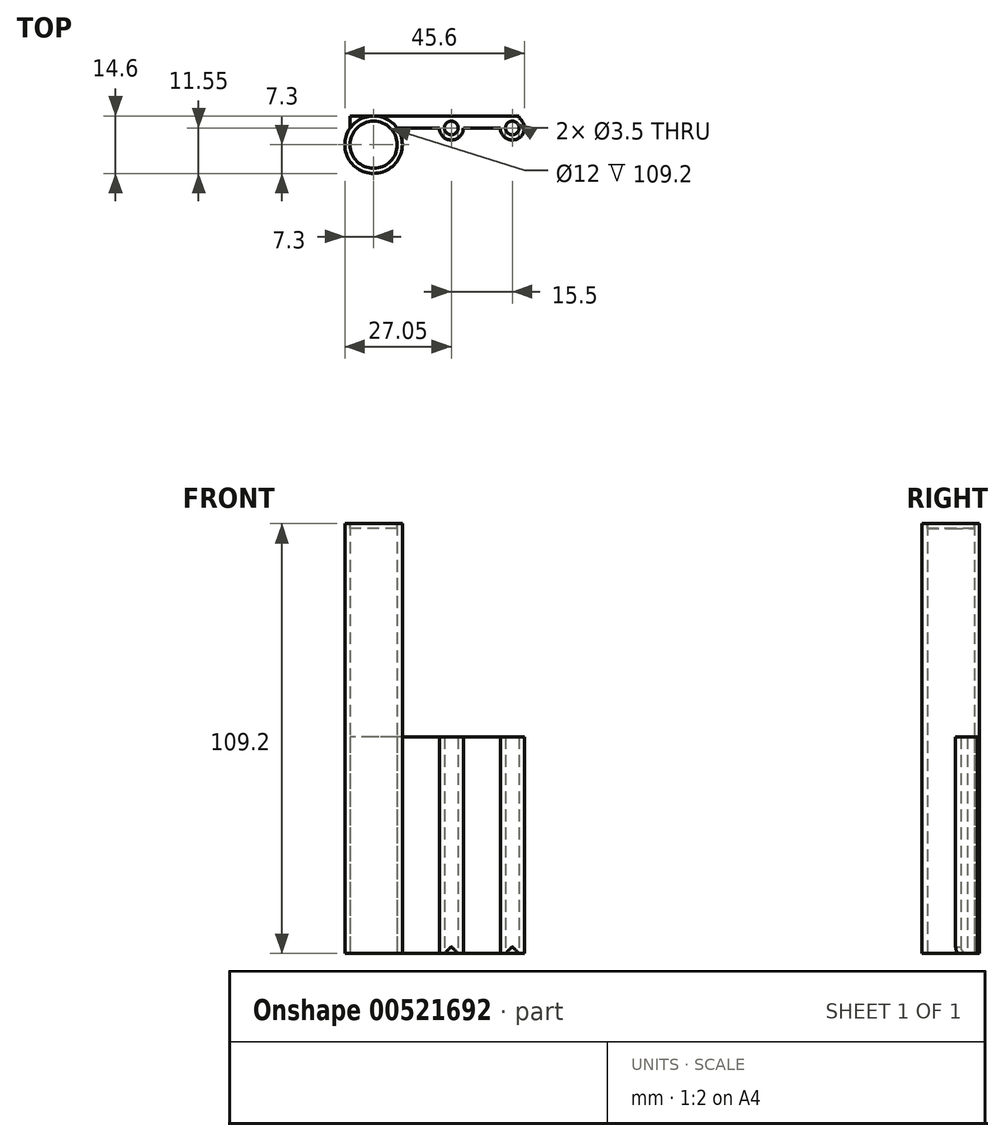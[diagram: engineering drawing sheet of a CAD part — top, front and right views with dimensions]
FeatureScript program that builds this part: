
annotation { "Feature Type Name" : "Feature", "Feature Type Description" : "" }
export const myFeature = defineFeature(function(context is Context, id is Id, definition is map)
    precondition{}
    {
        {
            var Q0;
            Q0=qCreatedBy(makeId("Top.planeOp"),FACE);
            var sketch = newSketch(context, id + "F0", { "sketchPlane" : qUnion([Q0])});
            skLineSegment(sketch, "E0.MirrorCS", {"start": v(-1.3, -1.75) * mm, "end": v(-1.3, -1.84) * mm});
            skLineSegment(sketch, "E1.MirrorCS", {"start": v(29.7, 0.75) * mm, "end": v(29.7, 1.3) * mm});
            skLineSegment(sketch, "E2.MirrorCS", {"start": v(9.4, -1.75) * mm, "end": v(-1.3, -1.75) * mm});
            skLineSegment(sketch, "E3.MirrorCS", {"start": v(-13.3, -1.84) * mm, "end": v(-13.3, 1.3) * mm});
            skArc(sketch, "E4.MirrorCS", {"start": v(-1.3, -1.84) * mm, "mid": v(-7.3, -13.3) * mm, "end": v(-13.3, -1.84) * mm});
            skCircle(sketch, "E5.MirrorC", {"center": v(-7.3, -6) * mm, "radius": 6 * mm});
            skLineSegment(sketch, "E6.MirrorCS", {"start": v(24.9, -1.75) * mm, "end": v(15.5, -1.75) * mm});
            skArc(sketch, "E7.MirrorCS", {"start": v(29.7, 0.75) * mm, "mid": v(29.36, -4.46) * mm, "end": v(24.9, -1.75) * mm});
            skLineSegment(sketch, "E8.MirrorCS", {"start": v(29.7, 1.3) * mm, "end": v(-13.3, 1.3) * mm});
            skCircle(sketch, "E9.MirrorC", {"center": v(27.95, -1.75) * mm, "radius": 1.75 * mm});
            skCircle(sketch, "E10.MirrorC", {"center": v(12.45, -1.75) * mm, "radius": 1.75 * mm});
            skArc(sketch, "E11.MirrorCS", {"start": v(9.4, -1.75) * mm, "mid": v(12.45, -4.8) * mm, "end": v(15.5, -1.75) * mm});
            skSolve(sketch);
        }
        {
            var Q0;
            Q0 = qSketchRegion(id + "F0", true);
            extrude(context, id + "F1", {"entities" : qUnion([Q0]), "depth" : 109.2 * mm, "offsetDistance" : 25 * mm});
        }
        {
            var Q0;
            Q0=makeQuery(id+"F1.opExtrude","SWEPT_FACE",FACE,{"disambiguationData":[OSD([sQuery(id+"F0.wireOp",EDGE,"E2.MirrorCS")])]});
            var sketch = newSketch(context, id + "F2", { "sketchPlane" : qUnion([Q0])});
            skLineSegment(sketch, "E12", {"start": v(10.7, 0) * mm, "end": v(12.45, 1.75) * mm});
            skLineSegment(sketch, "E13", {"start": v(12.45, 1.75) * mm, "end": v(14.2, 0) * mm});
            skLineSegment(sketch, "E14", {"start": v(10.7, 0) * mm, "end": v(14.2, 0) * mm});
            skLineSegment(sketch, "E15", {"start": v(26.2, 0) * mm, "end": v(27.95, 1.75) * mm});
            skLineSegment(sketch, "E16", {"start": v(27.95, 1.75) * mm, "end": v(29.7, 0) * mm});
            skLineSegment(sketch, "E17", {"start": v(29.7, 0) * mm, "end": v(26.2, 0) * mm});
            skSolve(sketch);
        }
        {
            var Q0;
            Q0 = qSketchRegion(id + "F2", true);
            extrude(context, id + "F3", {"entities" : qUnion([Q0]), "operationType" : NewBodyOperationType.REMOVE, "depth" : 25 * mm, "offsetDistance" : 25 * mm});
        }
        {
            var Q0;
            Q0=makeQuery(id+"F1.opExtrude","CAP_FACE",FACE,{"disambiguationData":[OSD([sQuery(id+"F0.wireOp",EDGE,"E0.MirrorCS"),sQuery(id+"F0.wireOp",EDGE,"E1.MirrorCS"),sQuery(id+"F0.wireOp",EDGE,"E2.MirrorCS"),sQuery(id+"F0.wireOp",EDGE,"E3.MirrorCS"),sQuery(id+"F0.wireOp",EDGE,"E4.MirrorCS"),sQuery(id+"F0.wireOp",EDGE,"E5.MirrorC"),sQuery(id+"F0.wireOp",EDGE,"E6.MirrorCS"),sQuery(id+"F0.wireOp",EDGE,"E7.MirrorCS"),sQuery(id+"F0.wireOp",EDGE,"E8.MirrorCS"),sQuery(id+"F0.wireOp",EDGE,"E9.MirrorC"),sQuery(id+"F0.wireOp",EDGE,"E10.MirrorC"),sQuery(id+"F0.wireOp",EDGE,"E11.MirrorCS")])],"isStart":false});
            var sketch = newSketch(context, id + "F4", { "sketchPlane" : qUnion([Q0])});
            skLineSegment(sketch, "E18.bottom", {"start": v(-18.39, 5.38) * mm, "end": v(33.57, 5.38) * mm});
            skLineSegment(sketch, "E18.top", {"start": v(-18.39, -16.44) * mm, "end": v(33.57, -16.44) * mm});
            skLineSegment(sketch, "E18.left", {"start": v(-18.39, 5.38) * mm, "end": v(-18.39, -16.44) * mm});
            skLineSegment(sketch, "E18.right", {"start": v(33.57, 5.38) * mm, "end": v(33.57, -16.44) * mm});
            skCircle(sketch, "E19", {"center": v(-7.3, -6) * mm, "radius": 7.3 * mm});
            skSolve(sketch);
        }
        {
            var Q0;
            Q0 = qSketchRegion(id + "F4", true);
            extrude(context, id + "F5", {"entities" : qUnion([Q0]), "operationType" : NewBodyOperationType.REMOVE, "oppositeDirection" : true, "depth" : 54.2 * mm, "offsetDistance" : 25 * mm});
        }
        {
            var Q0;
            Q0=makeQuery(id+"F1.opExtrude","CAP_FACE",FACE,{"disambiguationData":[OSD([sQuery(id+"F0.wireOp",EDGE,"E0.MirrorCS"),sQuery(id+"F0.wireOp",EDGE,"E1.MirrorCS"),sQuery(id+"F0.wireOp",EDGE,"E2.MirrorCS"),sQuery(id+"F0.wireOp",EDGE,"E3.MirrorCS"),sQuery(id+"F0.wireOp",EDGE,"E4.MirrorCS"),sQuery(id+"F0.wireOp",EDGE,"E5.MirrorC"),sQuery(id+"F0.wireOp",EDGE,"E6.MirrorCS"),sQuery(id+"F0.wireOp",EDGE,"E7.MirrorCS"),sQuery(id+"F0.wireOp",EDGE,"E8.MirrorCS"),sQuery(id+"F0.wireOp",EDGE,"E9.MirrorC"),sQuery(id+"F0.wireOp",EDGE,"E10.MirrorC"),sQuery(id+"F0.wireOp",EDGE,"E11.MirrorCS")])],"isStart":false});
            var sketch = newSketch(context, id + "F6", { "sketchPlane" : qUnion([Q0])});
            skCircle(sketch, "E20", {"center": v(-7.3, -6) * mm, "radius": 6 * mm});
            skSolve(sketch);
        }
        {
            var Q0;
            Q0 = qSketchRegion(id + "F6", true);
            extrude(context, id + "F7", {"entities" : qUnion([Q0]), "oppositeDirection" : true, "depth" : 1.2 * mm, "offsetDistance" : 25 * mm});
        }
    });
